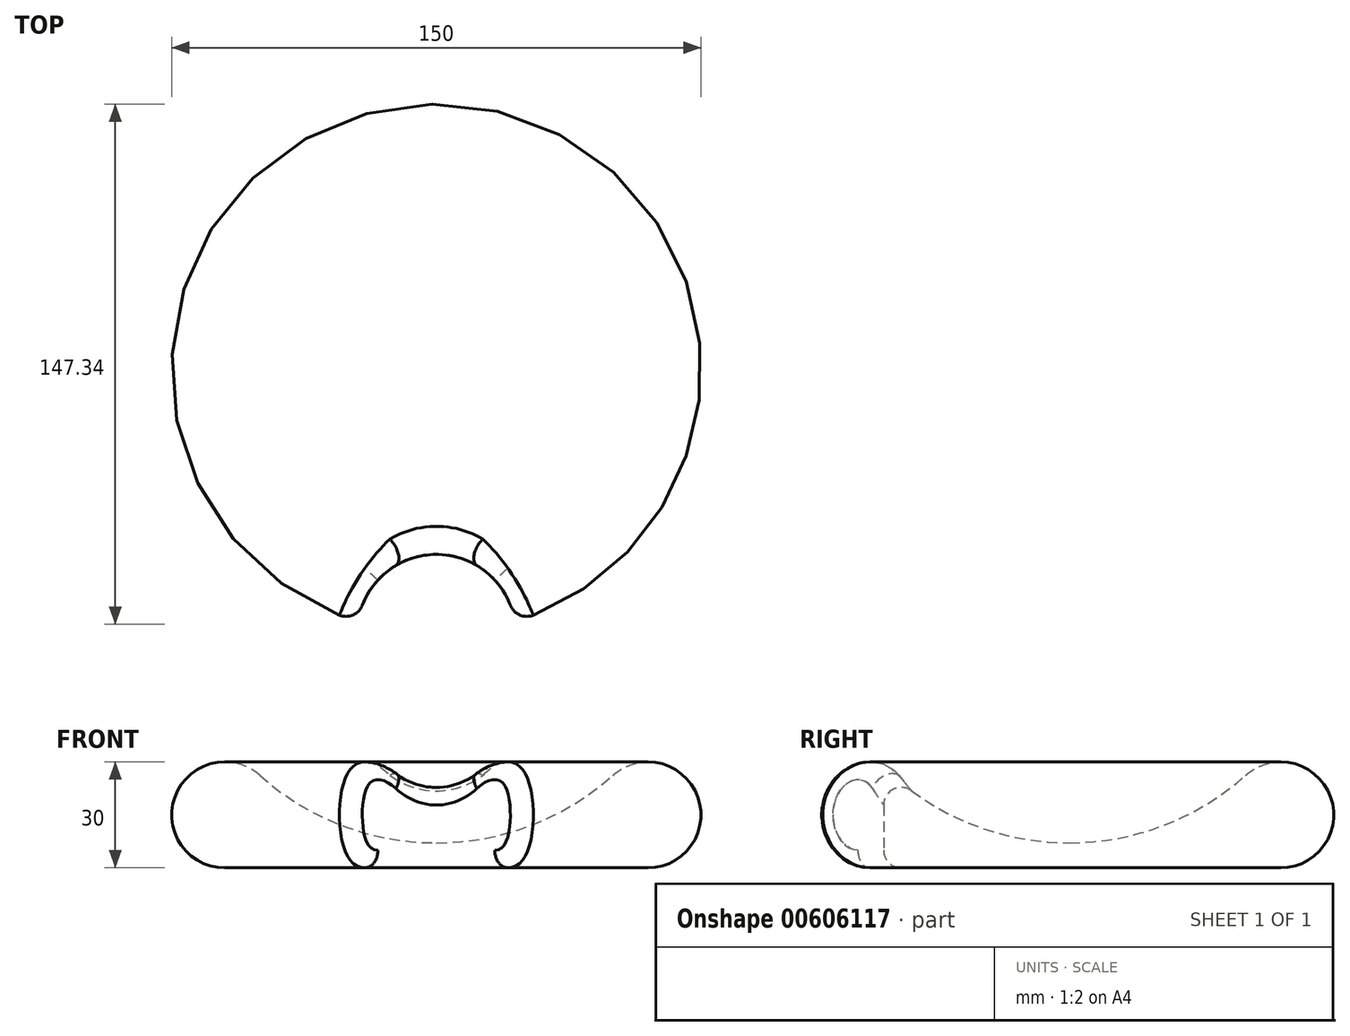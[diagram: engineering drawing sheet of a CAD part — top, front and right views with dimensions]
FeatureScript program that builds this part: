
annotation { "Feature Type Name" : "Feature", "Feature Type Description" : "" }
export const myFeature = defineFeature(function(context is Context, id is Id, definition is map)
    precondition{}
    {
        {
            var Q0;
            Q0=qCreatedBy(makeId("Front.planeOp"),FACE);
            var sketch = newSketch(context, id + "F0", { "sketchPlane" : qUnion([Q0])});
            skArc(sketch, "E0", {"start": v(-50, 35.47) * mm, "mid": v(-74.01, 29.64) * mm, "end": v(-60, 9.29) * mm});
            skArc(sketch, "E1", {"start": v(-50, 35.47) * mm, "mid": v(-26.76, 21.3) * mm, "end": v(0, 16.37) * mm});
            skLineSegment(sketch, "E2", {"start": v(-60, 9.29) * mm, "end": v(0, 9.29) * mm});
            skLineSegment(sketch, "E3", {"start": v(0, 9.29) * mm, "end": v(0, 16.37) * mm});
            skSolve(sketch);
        }
        {
            var Q0;
            Q0=makeQuery(id+"F0.imprint","IMPRINT",FACE,{"disambiguationData":[TD([[makeQuery(id+"F0.imprint","IMPRINT",EDGE,{"derivedFrom":sQuery(id+"F0.wireOp",EDGE,"E0")}),1.0]])]});
            var Q1;
            Q1=sQuery(id+"F0.wireOp",EDGE,"E3");
            var Q2;
            Q2=sQuery(id+"F0.wireOp",EDGE,"E0");
            var Q3;
            Q3=sQuery(id+"F0.wireOp",EDGE,"E2");
            var Q4;
            Q4=sQuery(id+"F0.wireOp",EDGE,"E1");
            var Q5;
            Q5=sQuery(id+"F0.wireOp",EDGE,"E3");
            revolve(context, id + "F1", {"entities" : qUnion([Q0]), "surfaceEntities" : qUnion([Q1, Q2, Q3, Q4]), "axis" : qUnion([Q5]), "revolveType" : RevolveType.FULL});
        }
        {
            var Q0;
            Q0=qCreatedBy(makeId("Top.planeOp"),FACE);
            var sketch = newSketch(context, id + "F2", { "sketchPlane" : qUnion([Q0])});
            skCircle(sketch, "E4", {"center": v(0, -75.08) * mm, "radius": 22.5 * mm});
            skSolve(sketch);
        }
        {
            var Q0;
            Q0=makeQuery(id+"F2.imprint","IMPRINT",FACE,{"disambiguationData":[TD([[makeQuery(id+"F2.imprint","IMPRINT",EDGE,{"derivedFrom":sQuery(id+"F2.wireOp",EDGE,"E4")}),1.0]])]});
            var Q1;
            Q1=sQuery(id+"F2.wireOp",EDGE,"E4");
            extrude(context, id + "F3", {"entities" : qUnion([Q0]), "operationType" : NewBodyOperationType.REMOVE, "surfaceEntities" : qUnion([Q1]), "depth" : 50 * mm, "offsetDistance" : 25 * mm});
        }
        {
            var Q0;
            Q0=makeQuery(id+"F3.boolean.opBoolean","INTERSECT",EDGE,{"derivedFrom":[makeQuery(id+"F1.opRevolve","SWEPT_FACE",FACE,{"disambiguationData":[OSD([sQuery(id+"F0.wireOp",EDGE,"E0")])]}),makeQuery(id+"F3.opExtrude","SWEPT_FACE",FACE,{"disambiguationData":[OSD([sQuery(id+"F2.wireOp",EDGE,"E4")])]})]});
            fillet(context, id + "F4", {"entities" : qUnion([Q0]), "radius" : 5 * mm, "tangentPropagation" : true, "allowEdgeOverflow" : false});
        }
    });
